# Revit family: WAGNER_Кран_DN25-40
name_source: partatom
category: Арматура трубопроводов
revit_build: Autodesk Revit 2017 (Build: 20170118_1100(x64)
units: mm (PartAtom-declared; Revit-internal decimal feet)

## family parameters
Всегда вертикально = Да
Заголовок OmniClass = Pipework Fittings
На основе рабочей плоскости = Нет
Номер OmniClass = 23.60.30.11.14
Общий = Да
При загрузке вырезать с полостями = Нет
Размер круглого соединителя = Использовать диаметр
Тип детали = Вставляется

## types (1)
- Typ 3KH-PVC
    ADSK_URL документации изделия = https://ru.wagnergroup.com
    ADSK_URL страницы изделия = https://ru.wagnergroup.com
    ADSK_Версия Revit = Revit 2017
    ADSK_Версия семейства = Версия 1
    ADSK_Дата изменения = 19.07.20
    ADSK_Единица измерения = шт.
    ADSK_Завод-изготовитель = WAGNER
    ADSK_Код изделия = -
    ADSK_Марка = Typ 3KH-PVC
    ADSK_Материал = WAGNER_PVC_Кран
    ADSK_Наименование = Кран 3-х позиционный, PVC
    ADSK_Наименование краткое = Кран 3-х позиционный
    ADSK_Размер_Высота = 0 мм
    ADSK_Размер_Длина = 0 мм
    ADSK_Размер_Ширина = 0 мм
    COBie Category = Pipework Fittings
    Masterformat Code = 33 12 16
    Masterformat Title = Water Utility Distribution Valves
    OmniClass Code = 23-29 33 11 17
    OmniClass Title = Dry Pipe Valves
    UNSPSC Code = 40141600
    UNSPSC Title = Valves
    URL = www.wagner-russia.com
    Uniclass Code = Pr_65_54
    Uniclass Title = Valve products
    WAGNER_Variation = 1
    WAGNER_Артикул = AD-10-0925
    WAGNER_Название = Кран 3-х позиционный, PVC
    WAGNER_Температурный режим. = от -20℃ до +60℃
    WAGNER_Тип = Typ 3KH-PVC
    bimon.ru = bimon.ru
    Изготовитель = WAGNER
    Описание = Кран 3-х позиционный, PVC
